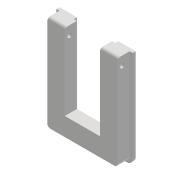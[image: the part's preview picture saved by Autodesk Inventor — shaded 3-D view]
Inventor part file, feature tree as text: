
AUTODESK INVENTOR PART (.ipt)
format: ipt  version: 2022 (Build 260153000, 153)  size: 152,576 bytes
history: native  units: mm
features: extrude x4, sketch x4, projected_geometry x2, fillet x1
ambient origin geometry x8: Origin, YZ Plane, XZ Plane, XY Plane, X Axis, Y Axis, Z Axis, Center Point
bodies: Volumenkörper1 (feature_tree)
feature tree (11):
  extrude  "Extrusion1"  Depth=23.0mm
  extrude  "Extrusion2"  Depth=50.0mm
  extrude  "Extrusion3"  Depth=46.0mm
  fillet  "Rundung1"  Radius=10.0mm
  extrude  "Extrusion4"  Depth=25.0mm TaperAngle=0.0deg
  sketch  "Skizze1"  dims[d0=23.0mm d1=76.0mm]
  sketch  "Skizze2"  dims[d2=12.0mm d3=50.0mm]
  sketch  "Skizze3"  dims[d4=50.0mm d5=46.0mm d6=10.0mm d7=0.0mm]
  projected_geometry  "Projizierte Kontur1"
  sketch  "Skizze4"  dims[d8=0.5mm d9=25.0mm d10=0.0mm d11=3.0mm d12=10.0mm d13=0.0mm d14=2.0mm d15=2.0mm d16=2.0mm d17=0.0mm d18=2.0mm d19=2.0mm d20=0.0mm]
  projected_geometry  "Projizierte Kontur2"
